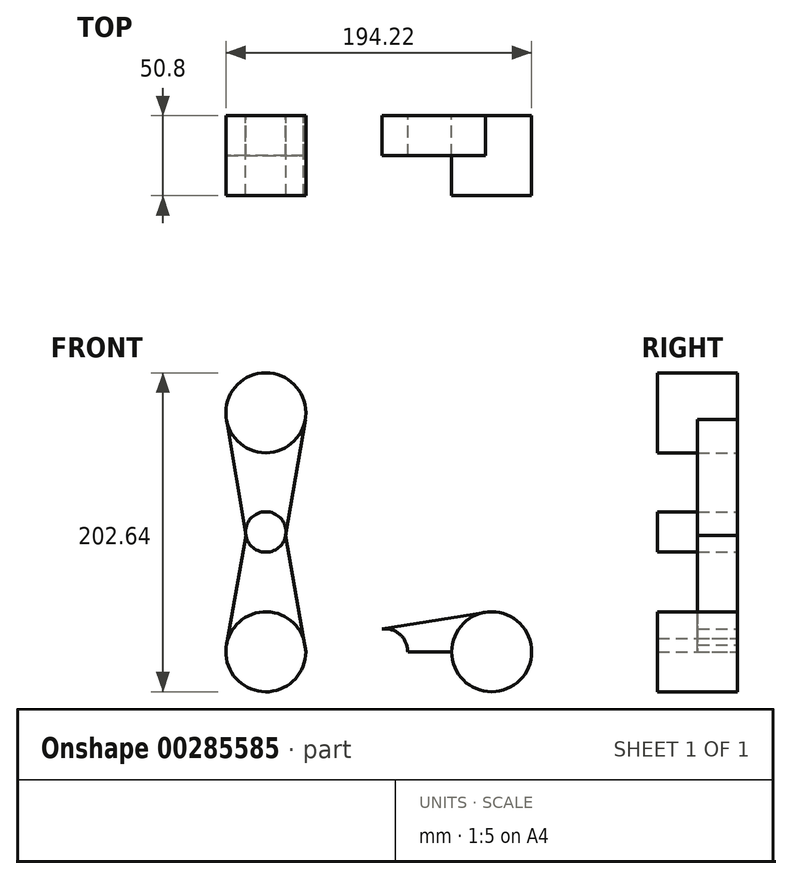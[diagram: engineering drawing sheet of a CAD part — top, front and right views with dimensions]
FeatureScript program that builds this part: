
annotation { "Feature Type Name" : "Feature", "Feature Type Description" : "" }
export const myFeature = defineFeature(function(context is Context, id is Id, definition is map)
    precondition{}
    {
        {
            var Q0;
            Q0=qCreatedBy(makeId("Front.planeOp"),FACE);
            var sketch = newSketch(context, id + "F0", { "sketchPlane" : qUnion([Q0])});
            skLineSegment(sketch, "E0", {"start": v(-211.92, 0) * mm, "end": v(-119.3, 0) * mm});
            skLineSegment(sketch, "E1", {"start": v(-119.3, 0) * mm, "end": v(-68.5, 0) * mm});
            skLineSegment(sketch, "E2", {"start": v(-182.88, 0) * mm, "end": v(-165.6, 0) * mm});
            skLineSegment(sketch, "E3", {"start": v(-165.6, 0) * mm, "end": v(-119.3, 0) * mm});
            skLineSegment(sketch, "E4", {"start": v(-211.92, 0) * mm, "end": v(-211.92, 76.12) * mm});
            skLineSegment(sketch, "E5", {"start": v(-211.92, 76.12) * mm, "end": v(-211.92, 151.84) * mm});
            skCircle(sketch, "E6", {"center": v(-211.92, 151.84) * mm, "radius": 25.4 * mm});
            skCircle(sketch, "E7", {"center": v(-68.5, 0) * mm, "radius": 25.4 * mm});
            skCircle(sketch, "E8", {"center": v(-211.92, 0) * mm, "radius": 25.4 * mm});
            skCircle(sketch, "E9", {"center": v(-211.92, 76.12) * mm, "radius": 12.82 * mm});
            skCircle(sketch, "E10", {"center": v(-136.48, 0) * mm, "radius": 14.69 * mm});
            skLineSegment(sketch, "E11", {"start": v(-236.96, 147.62) * mm, "end": v(-224.56, 74) * mm});
            skLineSegment(sketch, "E12", {"start": v(-186.87, 147.62) * mm, "end": v(-199.27, 74) * mm});
            skLineSegment(sketch, "E13", {"start": v(-224.56, 74) * mm, "end": v(-237.72, 0) * mm});
            skLineSegment(sketch, "E14", {"start": v(-199.27, 74) * mm, "end": v(-186.52, 0) * mm});
            skLineSegment(sketch, "E15", {"start": v(-187.98, 8.5) * mm, "end": v(-138.26, 14.58) * mm});
            skLineSegment(sketch, "E16", {"start": v(-138.26, 14.58) * mm, "end": v(-72.5, 25.08) * mm});
            skLineSegment(sketch, "E17", {"start": v(-199.27, -22.03) * mm, "end": v(-134.8, -14.59) * mm});
            skLineSegment(sketch, "E18", {"start": v(-134.8, -14.59) * mm, "end": v(-68.5, -25.76) * mm});
            skSolve(sketch);
        }
        {
            var Q0;
            {var subQ0=sQuery(id+"F0.wireOp",EDGE,"E6");var subQ1=makeQuery(id+"F0.imprint","INTERSECT",VERTEX,{"derivedFrom":[subQ0,sQuery(id+"F0.wireOp",EDGE,"E11")]});Q0=makeQuery(id+"F0.imprint","IMPRINT",FACE,{"disambiguationData":[TD([[makeQuery(id+"F0.imprint","IMPRINT",EDGE,{"disambiguationData":[TD([[subQ1,-1.0]])],"derivedFrom":subQ0}),1.0]])]});}
            var Q1;
            {var subQ0=sQuery(id+"F0.wireOp",EDGE,"E5");var subQ1=sQuery(id+"F0.wireOp",EDGE,"E4");var subQ2=makeQuery(id+"F0.imprint","INTERSECT",VERTEX,{"derivedFrom":[subQ1,subQ0]});Q1=makeQuery(id+"F0.imprint","IMPRINT",FACE,{"disambiguationData":[TD([[makeQuery(id+"F0.imprint","IMPRINT",EDGE,{"disambiguationData":[TD([[subQ2,1.0]])],"derivedFrom":subQ1}),-1.0]])]});}
            var Q2;
            {var subQ0=sQuery(id+"F0.wireOp",EDGE,"E5");var subQ1=sQuery(id+"F0.wireOp",EDGE,"E4");var subQ2=makeQuery(id+"F0.imprint","INTERSECT",VERTEX,{"derivedFrom":[subQ1,subQ0]});Q2=makeQuery(id+"F0.imprint","IMPRINT",FACE,{"disambiguationData":[TD([[makeQuery(id+"F0.imprint","IMPRINT",EDGE,{"disambiguationData":[TD([[subQ2,1.0]])],"derivedFrom":subQ1}),1.0]])]});}
            var Q3;
            {var subQ3=sQuery(id+"F0.wireOp",EDGE,"E4");var subQ4=sQuery(id+"F0.wireOp",EDGE,"E0");var subQ5=makeQuery(id+"F0.imprint","INTERSECT",VERTEX,{"derivedFrom":[subQ4,subQ3]});Q3=makeQuery(id+"F0.imprint","IMPRINT",FACE,{"disambiguationData":[TD([[makeQuery(id+"F0.imprint","IMPRINT",EDGE,{"disambiguationData":[TD([[subQ5,-1.0]])],"derivedFrom":subQ3}),1.0]])]});}
            var Q4;
            {var subQ0=sQuery(id+"F0.wireOp",EDGE,"E4");var subQ1=sQuery(id+"F0.wireOp",EDGE,"E0");var subQ2=makeQuery(id+"F0.imprint","INTERSECT",VERTEX,{"derivedFrom":[subQ1,subQ0]});Q4=makeQuery(id+"F0.imprint","IMPRINT",FACE,{"disambiguationData":[TD([[makeQuery(id+"F0.imprint","IMPRINT",EDGE,{"disambiguationData":[TD([[subQ2,-1.0]])],"derivedFrom":subQ0}),-1.0]])]});}
            var Q5;
            {var subQ0=sQuery(id+"F0.wireOp",EDGE,"E10");var subQ1=sQuery(id+"F0.wireOp",EDGE,"E3");var subQ2=makeQuery(id+"F0.imprint","INTERSECT",VERTEX,{"disambiguationData":[OD(0.0)],"derivedFrom":[subQ1,subQ0]});Q5=makeQuery(id+"F0.imprint","IMPRINT",FACE,{"disambiguationData":[TD([[makeQuery(id+"F0.imprint","IMPRINT",EDGE,{"disambiguationData":[TD([[subQ2,-1.0]])],"derivedFrom":subQ1}),1.0]])]});}
            var Q6;
            {var subQ0=sQuery(id+"F0.wireOp",EDGE,"E10");var subQ1=sQuery(id+"F0.wireOp",EDGE,"E3");var subQ2=makeQuery(id+"F0.imprint","INTERSECT",VERTEX,{"disambiguationData":[OD(0.0)],"derivedFrom":[subQ1,subQ0]});Q6=makeQuery(id+"F0.imprint","IMPRINT",FACE,{"disambiguationData":[TD([[makeQuery(id+"F0.imprint","IMPRINT",EDGE,{"disambiguationData":[TD([[subQ2,-1.0]])],"derivedFrom":subQ1}),-1.0]])]});}
            var Q7;
            {var subQ0=sQuery(id+"F0.wireOp",EDGE,"E7");var subQ1=makeQuery(id+"F0.imprint","INTERSECT",VERTEX,{"derivedFrom":[subQ0,sQuery(id+"F0.wireOp",EDGE,"E16")]});Q7=makeQuery(id+"F0.imprint","IMPRINT",FACE,{"disambiguationData":[TD([[makeQuery(id+"F0.imprint","IMPRINT",EDGE,{"disambiguationData":[TD([[subQ1,-1.0]])],"derivedFrom":subQ0}),1.0]])]});}
            extrude(context, id + "F1", {"entities" : qUnion([Q0, Q1, Q2, Q3, Q4, Q5, Q6, Q7]), "depth" : 50.8 * mm});
        }
        {
            var Q0;
            {var subQ5=sQuery(id+"F0.wireOp",EDGE,"E11");Q0=makeQuery(id+"F0.imprint","IMPRINT",FACE,{"disambiguationData":[TD([[makeQuery(id+"F0.imprint","IMPRINT",EDGE,{"derivedFrom":subQ5}),1.0]])]});}
            var Q1;
            {var subQ5=sQuery(id+"F0.wireOp",EDGE,"E12");Q1=makeQuery(id+"F0.imprint","IMPRINT",FACE,{"disambiguationData":[TD([[makeQuery(id+"F0.imprint","IMPRINT",EDGE,{"derivedFrom":subQ5}),-1.0]])]});}
            var Q2;
            {var subQ0=sQuery(id+"F0.wireOp",EDGE,"E8");var subQ1=sQuery(id+"F0.wireOp",EDGE,"E4");var subQ2=makeQuery(id+"F0.imprint","INTERSECT",VERTEX,{"derivedFrom":[subQ1,subQ0]});Q2=makeQuery(id+"F0.imprint","IMPRINT",FACE,{"disambiguationData":[TD([[makeQuery(id+"F0.imprint","IMPRINT",EDGE,{"disambiguationData":[TD([[subQ2,-1.0]])],"derivedFrom":subQ1}),-1.0]])]});}
            var Q3;
            {var subQ0=sQuery(id+"F0.wireOp",EDGE,"E8");var subQ1=sQuery(id+"F0.wireOp",EDGE,"E4");var subQ2=makeQuery(id+"F0.imprint","INTERSECT",VERTEX,{"derivedFrom":[subQ1,subQ0]});Q3=makeQuery(id+"F0.imprint","IMPRINT",FACE,{"disambiguationData":[TD([[makeQuery(id+"F0.imprint","IMPRINT",EDGE,{"disambiguationData":[TD([[subQ2,-1.0]])],"derivedFrom":subQ1}),1.0]])]});}
            var Q4;
            {var subQ3=sQuery(id+"F0.wireOp",EDGE,"E1");var subQ5=sQuery(id+"F0.wireOp",EDGE,"E3");var subQ6=makeQuery(id+"F0.imprint","INTERSECT",VERTEX,{"derivedFrom":[subQ5,subQ3]});Q4=makeQuery(id+"F0.imprint","IMPRINT",FACE,{"disambiguationData":[TD([[makeQuery(id+"F0.imprint","IMPRINT",EDGE,{"disambiguationData":[TD([[subQ6,1.0]])],"derivedFrom":subQ5}),-1.0]])]});}
            var Q5;
            {var subQ0=sQuery(id+"F0.wireOp",EDGE,"E16");Q5=makeQuery(id+"F0.imprint","IMPRINT",FACE,{"disambiguationData":[TD([[makeQuery(id+"F0.imprint","IMPRINT",EDGE,{"derivedFrom":subQ0}),-1.0]])]});}
            var Q6;
            {var subQ6=sQuery(id+"F0.wireOp",EDGE,"E2");Q6=makeQuery(id+"F0.imprint","IMPRINT",FACE,{"disambiguationData":[TD([[makeQuery(id+"F0.imprint","IMPRINT",EDGE,{"derivedFrom":subQ6}),1.0]])]});}
            var Q7;
            {var subQ1=sQuery(id+"F0.wireOp",EDGE,"E2");Q7=makeQuery(id+"F0.imprint","IMPRINT",FACE,{"disambiguationData":[TD([[makeQuery(id+"F0.imprint","IMPRINT",EDGE,{"derivedFrom":subQ1}),-1.0]])]});}
            extrude(context, id + "F2", {"entities" : qUnion([Q0, Q1, Q2, Q3, Q4, Q5, Q6, Q7]), "depth" : 25.4 * mm});
        }
    });
